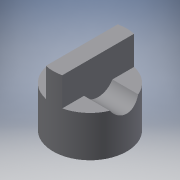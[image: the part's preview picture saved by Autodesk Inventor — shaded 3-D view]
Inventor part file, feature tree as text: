
AUTODESK INVENTOR PART (.ipt)
format: ipt  version: 2016 (Build 200138000, 138)  size: 143,872 bytes
history: native  units: in
note: dims shown in document units (in); Inventor stores cm internally (conversion verified against a paired STEP export)
features: extrude x5, sketch x5, projected_geometry x2, fillet x1
ambient origin geometry x8: Origin, YZ Plane, XZ Plane, XY Plane, X Axis, Y Axis, Z Axis, Center Point
bodies: Solid1 (feature_tree)
feature tree (13):
  extrude  "Extrusion1"  Depth=0.1969in TaperAngle=0.0deg
  extrude  "Extrusion2"  Depth=0.0394in
  extrude  "Extrusion3"  Depth=0.1969in TaperAngle=0.0deg
  extrude  "Extrusion7"  Depth=0.0394in
  extrude  "Extrusion8"  Depth=0.0394in
  fillet  "Fillet2"  Radius=1.0in
  sketch  "Sketch1"  dims[d0=0.3543in d1=0.1969in d2=0.0in]
  sketch  "Sketch2"  dims[d4=0.0394in d5=0.0787in]
  sketch  "Sketch3"  dims[d6=0.1969in d7=0.0in d8=0.1969in d9=0.0in]
  projected_geometry  "Projected Loop1"
  projected_geometry  "Projected Loop2"
  sketch  "Sketch7"  dims[d20=0.0394in d21=0.1575in]
  sketch  "Sketch8"  dims[d22=1.0in d23=0.0in d24=0.0591in d25=1.0in d26=0.0in d27=0.0394in]
